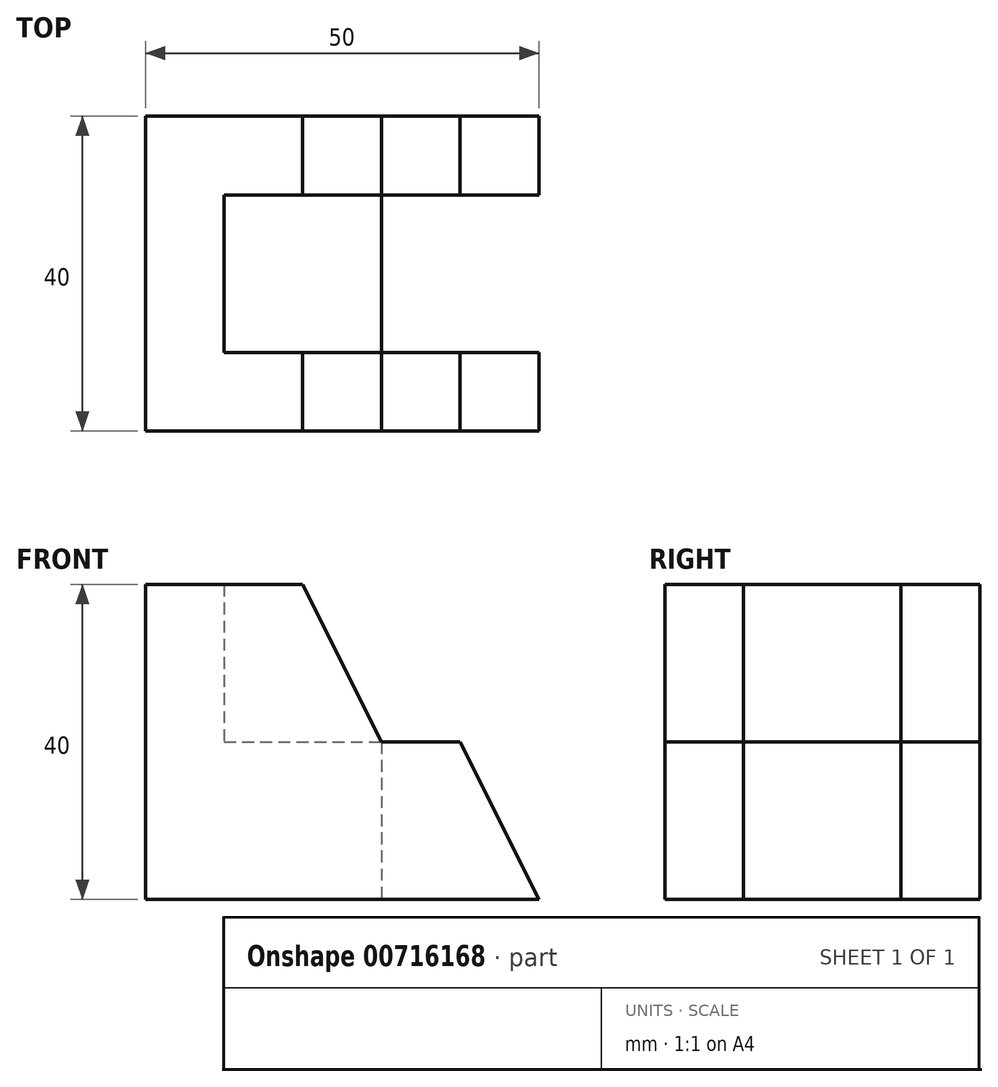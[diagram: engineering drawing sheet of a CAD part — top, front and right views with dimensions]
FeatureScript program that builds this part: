
annotation { "Feature Type Name" : "Feature", "Feature Type Description" : "" }
export const myFeature = defineFeature(function(context is Context, id is Id, definition is map)
    precondition{}
    {
        {
            var Q0;
            Q0=qCreatedBy(makeId("Front.planeOp"),FACE);
            var sketch = newSketch(context, id + "F0", { "sketchPlane" : qUnion([Q0])});
            skLineSegment(sketch, "E0", {"start": v(50, 0) * mm, "end": v(0, 0) * mm});
            skLineSegment(sketch, "E1", {"start": v(0, 0) * mm, "end": v(0, 40) * mm});
            skLineSegment(sketch, "E2", {"start": v(0, 40) * mm, "end": v(20, 40) * mm});
            skLineSegment(sketch, "E3", {"start": v(20, 40) * mm, "end": v(30, 20) * mm});
            skLineSegment(sketch, "E4", {"start": v(30, 20) * mm, "end": v(40, 20) * mm});
            skLineSegment(sketch, "E5", {"start": v(40, 20) * mm, "end": v(50, 0) * mm});
            skSolve(sketch);
        }
        {
            var Q0;
            Q0=makeQuery(id+"F0.imprint","IMPRINT",FACE,{"disambiguationData":[TD([[makeQuery(id+"F0.imprint","IMPRINT",EDGE,{"derivedFrom":sQuery(id+"F0.wireOp",EDGE,"E0")}),-1.0]])]});
            extrude(context, id + "F1", {"entities" : qUnion([Q0]), "endBound" : BoundingType.SYMMETRIC, "oppositeDirection" : true, "depth" : 40 * mm, "offsetDistance" : 25 * mm});
        }
        {
            var Q0;
            Q0=qCreatedBy(makeId("Front.planeOp"),FACE);
            var sketch = newSketch(context, id + "F2", { "sketchPlane" : qUnion([Q0])});
            skLineSegment(sketch, "E6", {"start": v(50, 0) * mm, "end": v(50, 40) * mm});
            skLineSegment(sketch, "E7", {"start": v(50, 40) * mm, "end": v(10, 40) * mm});
            skLineSegment(sketch, "E8", {"start": v(10, 40) * mm, "end": v(10, 20) * mm});
            skLineSegment(sketch, "E9", {"start": v(10, 20) * mm, "end": v(30, 20) * mm});
            skLineSegment(sketch, "E10", {"start": v(30, 20) * mm, "end": v(30, 0) * mm});
            skLineSegment(sketch, "E11", {"start": v(30, 0) * mm, "end": v(50, 0) * mm});
            skSolve(sketch);
        }
        {
            var Q0;
            Q0 = qSketchRegion(id + "F2", true);
            extrude(context, id + "F3", {"entities" : qUnion([Q0]), "operationType" : NewBodyOperationType.REMOVE, "endBound" : BoundingType.SYMMETRIC, "depth" : 20 * mm, "offsetDistance" : 25 * mm});
        }
    });
